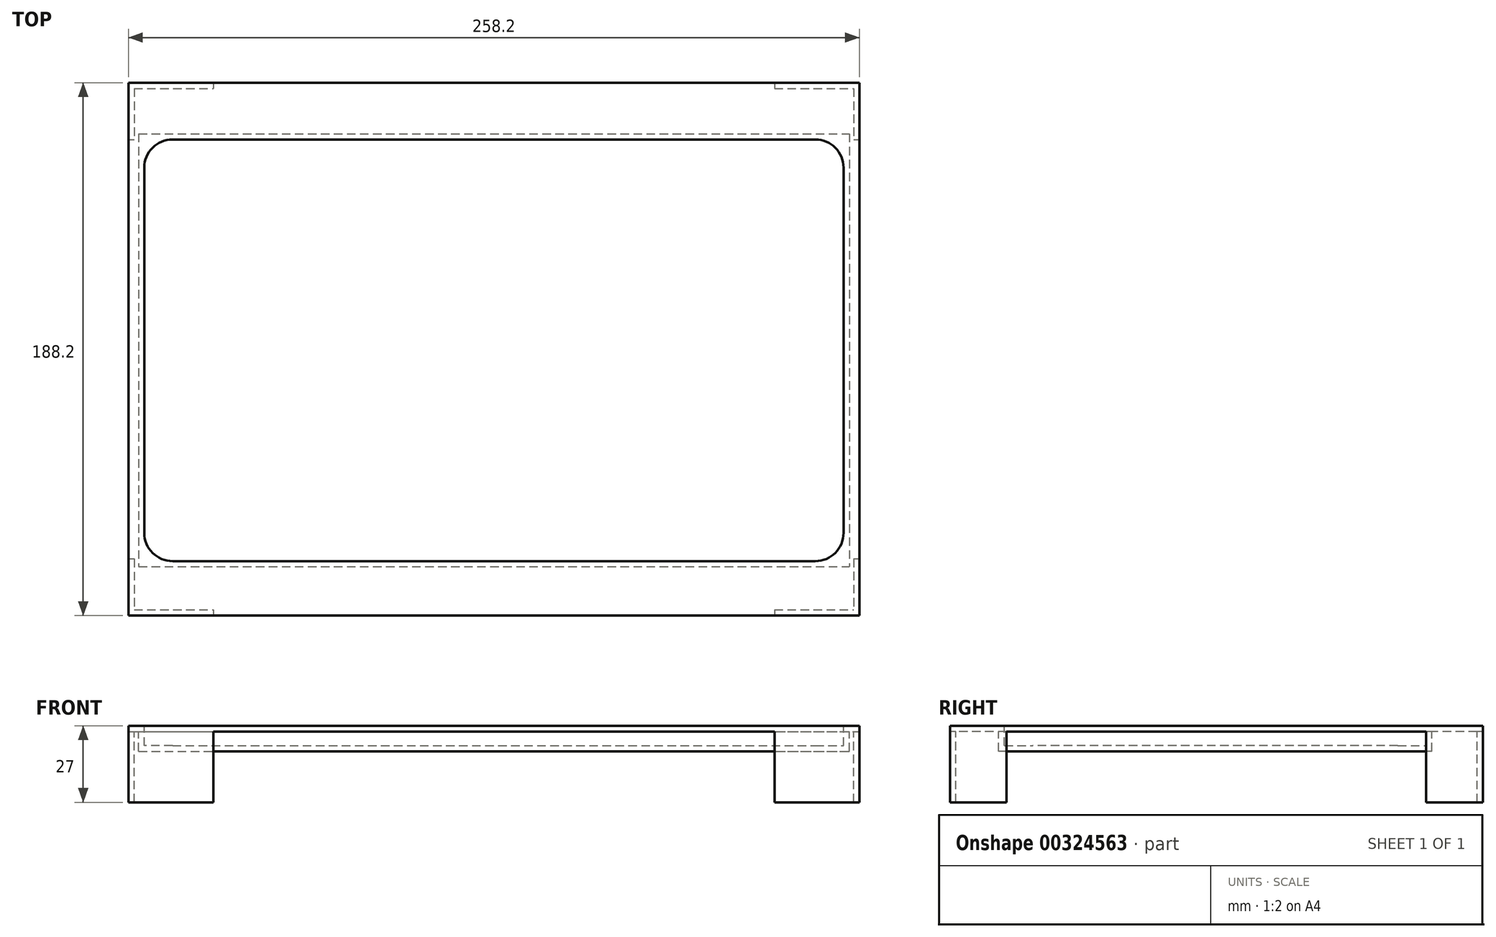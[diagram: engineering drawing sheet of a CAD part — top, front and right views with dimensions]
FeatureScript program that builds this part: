
annotation { "Feature Type Name" : "Feature", "Feature Type Description" : "" }
export const myFeature = defineFeature(function(context is Context, id is Id, definition is map)
    precondition{}
    {
        {
            var Q0;
            Q0=qCreatedBy(makeId("Top.planeOp"),FACE);
            var sketch = newSketch(context, id + "F0", { "sketchPlane" : qUnion([Q0])});
            skLineSegment(sketch, "E0.bottom", {"start": v(-127.1, 92.5) * mm, "end": v(127.1, 92.5) * mm});
            skLineSegment(sketch, "E0.top", {"start": v(-127.1, -91.7) * mm, "end": v(127.1, -91.7) * mm});
            skLineSegment(sketch, "E0.left", {"start": v(-127.1, 92.5) * mm, "end": v(-127.1, -91.7) * mm});
            skLineSegment(sketch, "E0.right", {"start": v(127.1, 92.5) * mm, "end": v(127.1, -91.7) * mm});
            skLineSegment(sketch, "E1.bottom", {"start": v(129.1, 94.5) * mm, "end": v(-129.1, 94.5) * mm});
            skLineSegment(sketch, "E1.top", {"start": v(129.1, -93.7) * mm, "end": v(-129.1, -93.7) * mm});
            skLineSegment(sketch, "E1.left", {"start": v(129.1, 94.5) * mm, "end": v(129.1, -93.7) * mm});
            skLineSegment(sketch, "E1.right", {"start": v(-129.1, 94.5) * mm, "end": v(-129.1, -93.7) * mm});
            skLineSegment(sketch, "E2", {"start": v(-99.1, 94.5) * mm, "end": v(-99.1, 92.5) * mm});
            skLineSegment(sketch, "E3", {"start": v(99.1, 94.5) * mm, "end": v(99.1, 92.5) * mm});
            skLineSegment(sketch, "E4", {"start": v(-129.1, 74.5) * mm, "end": v(-127.1, 74.5) * mm});
            skLineSegment(sketch, "E5", {"start": v(-129.1, -73.7) * mm, "end": v(-127.1, -73.7) * mm});
            skLineSegment(sketch, "E6", {"start": v(127.1, 74.5) * mm, "end": v(129.1, 74.5) * mm});
            skLineSegment(sketch, "E7", {"start": v(127.1, -73.67) * mm, "end": v(129.1, -73.7) * mm});
            skLineSegment(sketch, "E8", {"start": v(-99.1, -91.7) * mm, "end": v(-99.1, -93.7) * mm});
            skLineSegment(sketch, "E9", {"start": v(99.1, -91.7) * mm, "end": v(99.1, -93.7) * mm});
            skLineSegment(sketch, "E10.bottom", {"start": v(-113.5, 74.5) * mm, "end": v(113.5, 74.5) * mm});
            skLineSegment(sketch, "E10.top", {"start": v(-113.5, -74.5) * mm, "end": v(113.5, -74.5) * mm});
            skLineSegment(sketch, "E10.left", {"start": v(-123.5, 64.5) * mm, "end": v(-123.5, -64.5) * mm});
            skLineSegment(sketch, "E10.right", {"start": v(123.5, 64.5) * mm, "end": v(123.5, -64.5) * mm});
            skPoint(sketch, "E10.middle", {"position": v(0, 0) * mm});
            skLineSegment(sketch, "E11.bottom", {"start": v(-125.5, 76.5) * mm, "end": v(125.5, 76.5) * mm});
            skLineSegment(sketch, "E11.top", {"start": v(-125.5, -76.5) * mm, "end": v(125.5, -76.5) * mm});
            skLineSegment(sketch, "E11.left", {"start": v(-125.5, 76.5) * mm, "end": v(-125.5, -76.5) * mm});
            skLineSegment(sketch, "E11.right", {"start": v(125.5, 76.5) * mm, "end": v(125.5, -76.5) * mm});
            skPoint(sketch, "E12.visualSharp", {"position": v(-123.5, -74.5) * mm});
            skArc(sketch, "E12.filletArc", {"start": v(-123.5, -64.5) * mm, "mid": v(-120.57, -71.57) * mm, "end": v(-113.5, -74.5) * mm});
            skPoint(sketch, "E13.visualSharp", {"position": v(123.5, -74.5) * mm});
            skArc(sketch, "E13.filletArc", {"start": v(113.5, -74.5) * mm, "mid": v(120.57, -71.57) * mm, "end": v(123.5, -64.5) * mm});
            skPoint(sketch, "E14.visualSharp", {"position": v(123.5, 74.5) * mm});
            skArc(sketch, "E14.filletArc", {"start": v(123.5, 64.5) * mm, "mid": v(120.57, 71.57) * mm, "end": v(113.5, 74.5) * mm});
            skPoint(sketch, "E15.visualSharp", {"position": v(-123.5, 74.5) * mm});
            skArc(sketch, "E15.filletArc", {"start": v(-113.5, 74.5) * mm, "mid": v(-120.57, 71.57) * mm, "end": v(-123.5, 64.5) * mm});
            skSolve(sketch);
        }
        {
            var Q0;
            {var subQ7=sQuery(id+"F0.wireOp",EDGE,"E3");Q0=makeQuery(id+"F0.imprint","IMPRINT",FACE,{"disambiguationData":[TD([[makeQuery(id+"F0.imprint","IMPRINT",EDGE,{"derivedFrom":subQ7}),1.0]])]});}
            var Q1;
            {var subQ3=sQuery(id+"F0.wireOp",EDGE,"E7");Q1=makeQuery(id+"F0.imprint","IMPRINT",FACE,{"disambiguationData":[TD([[makeQuery(id+"F0.imprint","IMPRINT",EDGE,{"derivedFrom":subQ3}),-1.0]])]});}
            var Q2;
            {var subQ4=sQuery(id+"F0.wireOp",EDGE,"E5");Q2=makeQuery(id+"F0.imprint","IMPRINT",FACE,{"disambiguationData":[TD([[makeQuery(id+"F0.imprint","IMPRINT",EDGE,{"derivedFrom":subQ4}),-1.0]])]});}
            var Q3;
            {var subQ3=sQuery(id+"F0.wireOp",EDGE,"E2");Q3=makeQuery(id+"F0.imprint","IMPRINT",FACE,{"disambiguationData":[TD([[makeQuery(id+"F0.imprint","IMPRINT",EDGE,{"derivedFrom":subQ3}),-1.0]])]});}
            extrude(context, id + "F1", {"entities" : qUnion([Q0, Q1, Q2, Q3]), "depth" : -27 * mm});
        }
        {
            var Q0;
            Q0=makeQuery(id+"F0.imprint","IMPRINT",FACE,{"disambiguationData":[TD([[makeQuery(id+"F0.imprint","IMPRINT",EDGE,{"derivedFrom":sQuery(id+"F0.wireOp",EDGE,"E11.bottom")}),1.0]])]});
            var Q1;
            Q1=makeQuery(id+"F0.imprint","IMPRINT",FACE,{"disambiguationData":[TD([[makeQuery(id+"F0.imprint","IMPRINT",EDGE,{"derivedFrom":sQuery(id+"F0.wireOp",EDGE,"E10.bottom")}),1.0]])]});
            extrude(context, id + "F2", {"entities" : qUnion([Q0, Q1]), "operationType" : NewBodyOperationType.ADD, "depth" : -2 * mm});
        }
        {
            var Q0;
            {var subQ0=sQuery(id+"F0.wireOp",EDGE,"E8");Q0=makeQuery(id+"F0.imprint","IMPRINT",FACE,{"disambiguationData":[TD([[makeQuery(id+"F0.imprint","IMPRINT",EDGE,{"derivedFrom":subQ0}),1.0]])]});}
            var Q1;
            {var subQ0=sQuery(id+"F0.wireOp",EDGE,"E2");Q1=makeQuery(id+"F0.imprint","IMPRINT",FACE,{"disambiguationData":[TD([[makeQuery(id+"F0.imprint","IMPRINT",EDGE,{"derivedFrom":subQ0}),1.0]])]});}
            var Q2;
            {var subQ0=sQuery(id+"F0.wireOp",EDGE,"E4");Q2=makeQuery(id+"F0.imprint","IMPRINT",FACE,{"disambiguationData":[TD([[makeQuery(id+"F0.imprint","IMPRINT",EDGE,{"derivedFrom":subQ0}),-1.0]])]});}
            var Q3;
            {var subQ0=sQuery(id+"F0.wireOp",EDGE,"E6");Q3=makeQuery(id+"F0.imprint","IMPRINT",FACE,{"disambiguationData":[TD([[makeQuery(id+"F0.imprint","IMPRINT",EDGE,{"derivedFrom":subQ0}),-1.0]])]});}
            extrude(context, id + "F3", {"entities" : qUnion([Q0, Q1, Q2, Q3]), "operationType" : NewBodyOperationType.ADD, "depth" : -2 * mm});
        }
        {
            var Q0;
            Q0=makeQuery(id+"F0.imprint","IMPRINT",FACE,{"disambiguationData":[TD([[makeQuery(id+"F0.imprint","IMPRINT",EDGE,{"derivedFrom":sQuery(id+"F0.wireOp",EDGE,"E10.bottom")}),1.0]])]});
            var Q1;
            Q1=makeQuery(id+"F0.imprint","IMPRINT",FACE,{"disambiguationData":[TD([[makeQuery(id+"F0.imprint","IMPRINT",EDGE,{"derivedFrom":sQuery(id+"F0.wireOp",EDGE,"E10.bottom")}),-1.0]])]});
            extrude(context, id + "F4", {"entities" : qUnion([Q0, Q1]), "operationType" : NewBodyOperationType.ADD, "depth" : -9 * mm});
        }
        {
            var Q0;
            Q0=makeQuery(id+"F0.imprint","IMPRINT",FACE,{"disambiguationData":[TD([[makeQuery(id+"F0.imprint","IMPRINT",EDGE,{"derivedFrom":sQuery(id+"F0.wireOp",EDGE,"E10.bottom")}),-1.0]])]});
            extrude(context, id + "F5", {"entities" : qUnion([Q0]), "operationType" : NewBodyOperationType.REMOVE, "depth" : -7 * mm});
        }
    });
